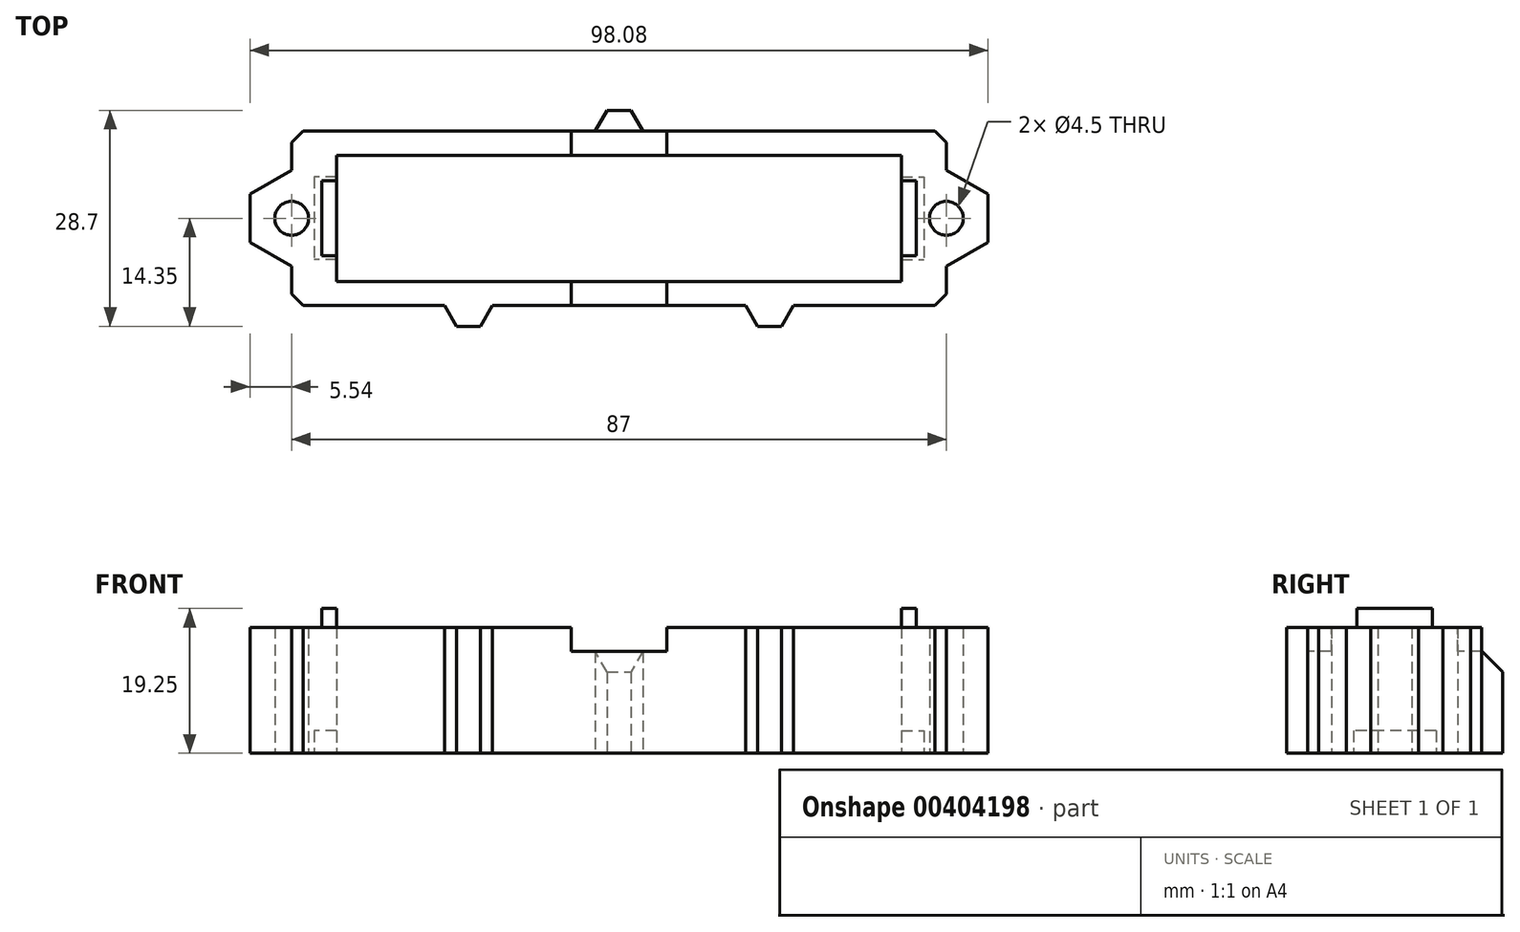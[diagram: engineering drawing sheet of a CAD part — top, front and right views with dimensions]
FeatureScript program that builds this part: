
annotation { "Feature Type Name" : "Feature", "Feature Type Description" : "" }
export const myFeature = defineFeature(function(context is Context, id is Id, definition is map)
    precondition{}
    {
        {
            var Q0;
            Q0=qCreatedBy(makeId("Top.planeOp"),FACE);
            var sketch = newSketch(context, id + "F0", { "sketchPlane" : qUnion([Q0])});
            skLineSegment(sketch, "E0.bottom", {"start": v(37.5, 8.37) * mm, "end": v(-37.5, 8.37) * mm});
            skLineSegment(sketch, "E0.top", {"start": v(37.5, -8.37) * mm, "end": v(-37.5, -8.37) * mm});
            skLineSegment(sketch, "E0.left", {"start": v(37.5, 8.37) * mm, "end": v(37.5, -8.37) * mm});
            skLineSegment(sketch, "E0.right", {"start": v(-37.5, 8.37) * mm, "end": v(-37.5, -8.37) * mm});
            skPoint(sketch, "E0.middle", {"position": v(0, 0) * mm});
            skLineSegment(sketch, "E1.bottom", {"start": v(43.5, 11.57) * mm, "end": v(2.77, 11.57) * mm});
            skLineSegment(sketch, "E1.top", {"start": v(43.5, -11.57) * mm, "end": v(23.2, -11.57) * mm});
            skLineSegment(sketch, "E1.left", {"start": v(43.5, 11.57) * mm, "end": v(43.5, 5.54) * mm});
            skLineSegment(sketch, "E1.right", {"start": v(-43.5, 11.57) * mm, "end": v(-43.5, 6.4) * mm});
            skCircle(sketch, "E2.cCircle", {"center": v(43.5, 0) * mm, "radius": 5.54 * mm, "construction": true});
            skPoint(sketch, "E2.cCircle.centerSnap0", {"position": v(43.5, 0) * mm});
            skLineSegment(sketch, "E2.0", {"start": v(49.04, 3.2) * mm, "end": v(49.04, -3.2) * mm});
            skLineSegment(sketch, "E2.1", {"start": v(49.04, -3.2) * mm, "end": v(43.5, -6.4) * mm});
            skLineSegment(sketch, "E2.2", {"start": v(43.5, -6.4) * mm, "end": v(37.96, -3.2) * mm, "construction": true});
            skLineSegment(sketch, "E2.3", {"start": v(37.96, -3.2) * mm, "end": v(37.96, 3.2) * mm, "construction": true});
            skLineSegment(sketch, "E2.4", {"start": v(37.96, 3.2) * mm, "end": v(43.5, 6.4) * mm, "construction": true});
            skLineSegment(sketch, "E2.5", {"start": v(43.5, 6.4) * mm, "end": v(49.04, 3.2) * mm});
            skPoint(sketch, "E2.0.midPoint", {"position": v(49.04, 0) * mm});
            skLineSegment(sketch, "E3.MirrorCS", {"start": v(-43.5, 6.4) * mm, "end": v(-49.04, 3.2) * mm});
            skLineSegment(sketch, "E4.MirrorCS", {"start": v(-49.04, 3.2) * mm, "end": v(-49.04, -3.2) * mm});
            skLineSegment(sketch, "E5.MirrorCS", {"start": v(-49.04, -3.2) * mm, "end": v(-43.5, -6.4) * mm});
            skLineSegment(sketch, "E6.trimOffspring", {"start": v(-43.5, -6.4) * mm, "end": v(-43.5, -11.57) * mm});
            skLineSegment(sketch, "E7.trimOffspring", {"start": v(43.5, -5.54) * mm, "end": v(43.5, -11.57) * mm});
            skCircle(sketch, "E8.cCircle", {"center": v(0, 11.57) * mm, "radius": 2.77 * mm, "construction": true});
            skLineSegment(sketch, "E8.0", {"start": v(-1.6, 14.35) * mm, "end": v(1.6, 14.35) * mm});
            skLineSegment(sketch, "E8.1", {"start": v(1.6, 14.35) * mm, "end": v(3.2, 11.57) * mm});
            skLineSegment(sketch, "E8.2", {"start": v(3.2, 11.57) * mm, "end": v(1.6, 8.8) * mm, "construction": true});
            skLineSegment(sketch, "E8.3", {"start": v(1.6, 8.8) * mm, "end": v(-1.6, 8.8) * mm, "construction": true});
            skLineSegment(sketch, "E8.4", {"start": v(-1.6, 8.8) * mm, "end": v(-3.2, 11.57) * mm, "construction": true});
            skLineSegment(sketch, "E8.5", {"start": v(-3.2, 11.57) * mm, "end": v(-1.6, 14.35) * mm});
            skPoint(sketch, "E8.0.midPoint", {"position": v(0, 14.35) * mm});
            skCircle(sketch, "E9.cCircle", {"center": v(-20, -11.57) * mm, "radius": 2.77 * mm, "construction": true});
            skLineSegment(sketch, "E9.0", {"start": v(-18.4, -14.35) * mm, "end": v(-21.6, -14.35) * mm});
            skLineSegment(sketch, "E9.1", {"start": v(-21.6, -14.35) * mm, "end": v(-23.2, -11.57) * mm});
            skLineSegment(sketch, "E9.2", {"start": v(-23.2, -11.57) * mm, "end": v(-21.6, -8.8) * mm, "construction": true});
            skLineSegment(sketch, "E9.3", {"start": v(-21.6, -8.8) * mm, "end": v(-18.4, -8.8) * mm, "construction": true});
            skLineSegment(sketch, "E9.4", {"start": v(-18.4, -8.8) * mm, "end": v(-16.8, -11.57) * mm, "construction": true});
            skLineSegment(sketch, "E9.5", {"start": v(-16.8, -11.57) * mm, "end": v(-18.4, -14.35) * mm});
            skPoint(sketch, "E9.0.midPoint", {"position": v(-20, -14.35) * mm});
            skLineSegment(sketch, "E10.MirrorCS", {"start": v(16.8, -11.57) * mm, "end": v(18.4, -14.35) * mm});
            skLineSegment(sketch, "E11.MirrorCS", {"start": v(21.6, -14.35) * mm, "end": v(23.2, -11.57) * mm});
            skLineSegment(sketch, "E12.MirrorCS", {"start": v(18.4, -14.35) * mm, "end": v(21.6, -14.35) * mm});
            skLineSegment(sketch, "E13.trimOffspring", {"start": v(16.8, -11.57) * mm, "end": v(-17.23, -11.57) * mm});
            skLineSegment(sketch, "E14.trimOffspring", {"start": v(-22.77, -11.57) * mm, "end": v(-43.5, -11.57) * mm});
            skLineSegment(sketch, "E15.trimOffspring", {"start": v(-2.77, 11.57) * mm, "end": v(-43.5, 11.57) * mm});
            skCircle(sketch, "E16", {"center": v(43.5, 0) * mm, "radius": 2.25 * mm});
            skCircle(sketch, "E17.MirrorC", {"center": v(-43.5, 0) * mm, "radius": 2.25 * mm});
            skSolve(sketch);
        }
        {
            var Q0;
            Q0=qSketchRegion(id+"F0",true);
            extrude(context, id + "F1", {"entities" : qUnion([Q0]), "depth" : 16.75 * mm});
        }
        {
            var Q0;
            Q0=makeQuery(id+"F1.opExtrude","SWEPT_EDGE",EDGE,{"disambiguationData":[OSD([sQuery(id+"F0.wireOp",EDGE,"E1.right"),sQuery(id+"F0.wireOp",EDGE,"E15.trimOffspring")])]});
            var Q1;
            Q1=makeQuery(id+"F1.opExtrude","SWEPT_EDGE",EDGE,{"disambiguationData":[OSD([sQuery(id+"F0.wireOp",EDGE,"E1.bottom"),sQuery(id+"F0.wireOp",EDGE,"E1.left")])]});
            var Q2;
            Q2=makeQuery(id+"F1.opExtrude","SWEPT_EDGE",EDGE,{"disambiguationData":[OSD([sQuery(id+"F0.wireOp",EDGE,"E1.top"),sQuery(id+"F0.wireOp",EDGE,"E7.trimOffspring")])]});
            var Q3;
            Q3=makeQuery(id+"F1.opExtrude","SWEPT_EDGE",EDGE,{"disambiguationData":[OSD([sQuery(id+"F0.wireOp",EDGE,"E6.trimOffspring"),sQuery(id+"F0.wireOp",EDGE,"E14.trimOffspring")])]});
            var Q4;
            Q4=makeQuery(id+"FqGxmhCherfDVOV_1.opExtrude","SWEPT_EDGE",EDGE,{"disambiguationData":[OSD([sQuery(id+"FbWVWexePYxeVdp_1.wireOp",EDGE,"DEU2wYtO-tHXI-QKIs-nlWb-i6qmyh1Z6pCu.bottom"),sQuery(id+"FbWVWexePYxeVdp_1.wireOp",EDGE,"DEU2wYtO-tHXI-QKIs-nlWb-i6qmyh1Z6pCu.right")])]});
            var Q5;
            Q5=makeQuery(id+"FqGxmhCherfDVOV_1.opExtrude","SWEPT_EDGE",EDGE,{"disambiguationData":[OSD([sQuery(id+"FbWVWexePYxeVdp_1.wireOp",EDGE,"DEU2wYtO-tHXI-QKIs-nlWb-i6qmyh1Z6pCu.bottom"),sQuery(id+"FbWVWexePYxeVdp_1.wireOp",EDGE,"DEU2wYtO-tHXI-QKIs-nlWb-i6qmyh1Z6pCu.left")])]});
            var Q6;
            Q6=makeQuery(id+"FqGxmhCherfDVOV_1.opExtrude","SWEPT_EDGE",EDGE,{"disambiguationData":[OSD([sQuery(id+"FbWVWexePYxeVdp_1.wireOp",EDGE,"DEU2wYtO-tHXI-QKIs-nlWb-i6qmyh1Z6pCu.top"),sQuery(id+"FbWVWexePYxeVdp_1.wireOp",EDGE,"f3f75a21-f88d-41ef-b49e-168493a3c54c.trimOffspring")])]});
            var Q7;
            Q7=makeQuery(id+"FqGxmhCherfDVOV_1.opExtrude","SWEPT_EDGE",EDGE,{"disambiguationData":[OSD([sQuery(id+"FbWVWexePYxeVdp_1.wireOp",EDGE,"DEU2wYtO-tHXI-QKIs-nlWb-i6qmyh1Z6pCu.top"),sQuery(id+"FbWVWexePYxeVdp_1.wireOp",EDGE,"1a49d25c-86bc-4509-88f6-b9e7389082c9.trimOffspring")])]});
            chamfer(context, id + "F2", {"entities" : qUnion([Q0, Q1, Q2, Q3, Q4, Q5, Q6, Q7]), "width" : 1.5 * mm, "tangentPropagation" : true});
        }
        {
            var Q0;
            Q0=qCreatedBy(makeId("Top.planeOp"),FACE);
            var sketch = newSketch(context, id + "F3", { "sketchPlane" : qUnion([Q0])});
            skLineSegment(sketch, "E18.bottom", {"start": v(-37.5, 5.5) * mm, "end": v(-40.5, 5.5) * mm});
            skLineSegment(sketch, "E18.top", {"start": v(-37.5, -5.5) * mm, "end": v(-40.5, -5.5) * mm});
            skLineSegment(sketch, "E18.left", {"start": v(-37.5, 5.5) * mm, "end": v(-37.5, -5.5) * mm});
            skLineSegment(sketch, "E18.right", {"start": v(-40.5, 5.5) * mm, "end": v(-40.5, -5.5) * mm});
            skPoint(sketch, "E18.middle", {"position": v(-39, 0) * mm});
            skLineSegment(sketch, "E19.MirrorCS", {"start": v(37.5, 5.5) * mm, "end": v(40.5, 5.5) * mm});
            skLineSegment(sketch, "E20.MirrorCS", {"start": v(37.5, -5.5) * mm, "end": v(40.5, -5.5) * mm});
            skLineSegment(sketch, "E21.MirrorCS", {"start": v(37.5, 5.5) * mm, "end": v(37.5, -5.5) * mm});
            skLineSegment(sketch, "E22.MirrorCS", {"start": v(40.5, 5.5) * mm, "end": v(40.5, -5.5) * mm});
            skPoint(sketch, "E23.MirrorP", {"position": v(39, 0) * mm});
            skSolve(sketch);
        }
        {
            var Q0;
            Q0=qSketchRegion(id+"F3",true);
            extrude(context, id + "F4", {"entities" : qUnion([Q0]), "operationType" : NewBodyOperationType.REMOVE, "depth" : 3 * mm});
        }
        {
            var Q0;
            Q0=makeQuery(id+"F1.opExtrude","CAP_FACE",FACE,{"disambiguationData":[OSD([sQuery(id+"F0.wireOp",EDGE,"E0.bottom"),sQuery(id+"F0.wireOp",EDGE,"E0.top"),sQuery(id+"F0.wireOp",EDGE,"E0.left"),sQuery(id+"F0.wireOp",EDGE,"E0.right"),sQuery(id+"F0.wireOp",EDGE,"E1.bottom"),sQuery(id+"F0.wireOp",EDGE,"E1.top"),sQuery(id+"F0.wireOp",EDGE,"E1.left"),sQuery(id+"F0.wireOp",EDGE,"E1.right"),sQuery(id+"F0.wireOp",EDGE,"E2.0"),sQuery(id+"F0.wireOp",EDGE,"E2.1"),sQuery(id+"F0.wireOp",EDGE,"E2.5"),sQuery(id+"F0.wireOp",EDGE,"E3.MirrorCS"),sQuery(id+"F0.wireOp",EDGE,"E4.MirrorCS"),sQuery(id+"F0.wireOp",EDGE,"E5.MirrorCS"),sQuery(id+"F0.wireOp",EDGE,"E6.trimOffspring"),sQuery(id+"F0.wireOp",EDGE,"E7.trimOffspring"),sQuery(id+"F0.wireOp",EDGE,"E8.0"),sQuery(id+"F0.wireOp",EDGE,"E8.1"),sQuery(id+"F0.wireOp",EDGE,"E8.5"),sQuery(id+"F0.wireOp",EDGE,"E9.0"),sQuery(id+"F0.wireOp",EDGE,"E9.1"),sQuery(id+"F0.wireOp",EDGE,"E9.5"),sQuery(id+"F0.wireOp",EDGE,"E10.MirrorCS"),sQuery(id+"F0.wireOp",EDGE,"E11.MirrorCS"),sQuery(id+"F0.wireOp",EDGE,"E12.MirrorCS"),sQuery(id+"F0.wireOp",EDGE,"E13.trimOffspring"),sQuery(id+"F0.wireOp",EDGE,"E14.trimOffspring"),sQuery(id+"F0.wireOp",EDGE,"E15.trimOffspring"),sQuery(id+"F0.wireOp",EDGE,"E16"),sQuery(id+"F0.wireOp",EDGE,"E17.MirrorC")])],"isStart":false});
            var sketch = newSketch(context, id + "F5", { "sketchPlane" : qUnion([Q0])});
            skLineSegment(sketch, "E24.bottom", {"start": v(-37.5, 5) * mm, "end": v(-39.5, 5) * mm});
            skLineSegment(sketch, "E24.top", {"start": v(-37.5, -5) * mm, "end": v(-39.5, -5) * mm});
            skLineSegment(sketch, "E24.left", {"start": v(-37.5, 5) * mm, "end": v(-37.5, -5) * mm});
            skLineSegment(sketch, "E24.right", {"start": v(-39.5, 5) * mm, "end": v(-39.5, -5) * mm});
            skPoint(sketch, "E24.middle", {"position": v(-38.5, 0) * mm});
            skPoint(sketch, "E24.middle.positionSnap0", {"position": v(-49.04, 0) * mm});
            skPoint(sketch, "E24.centerSnap0", {"position": v(-49.04, 0) * mm});
            skLineSegment(sketch, "E25.MirrorCS", {"start": v(37.5, 5) * mm, "end": v(39.5, 5) * mm});
            skLineSegment(sketch, "E26.MirrorCS", {"start": v(37.5, -5) * mm, "end": v(39.5, -5) * mm});
            skPoint(sketch, "E27.MirrorP", {"position": v(38.5, 0) * mm});
            skLineSegment(sketch, "E28.MirrorCS", {"start": v(39.5, 5) * mm, "end": v(39.5, -5) * mm});
            skLineSegment(sketch, "E29.MirrorCS", {"start": v(37.5, 5) * mm, "end": v(37.5, -5) * mm});
            skSolve(sketch);
        }
        {
            var Q0;
            Q0=qSketchRegion(id+"F5",true);
            extrude(context, id + "F6", {"entities" : qUnion([Q0]), "operationType" : NewBodyOperationType.ADD, "depth" : 2.5 * mm});
        }
        {
            var Q0;
            Q0=makeQuery(id+"F1.opExtrude","SWEPT_FACE",FACE,{"disambiguationData":[OSD([sQuery(id+"F0.wireOp",EDGE,"E13.trimOffspring")])]});
            var sketch = newSketch(context, id + "F7", { "sketchPlane" : qUnion([Q0])});
            skLineSegment(sketch, "E30.bottom", {"start": v(6.35, 13.55) * mm, "end": v(-6.35, 13.55) * mm});
            skLineSegment(sketch, "E30.top", {"start": v(6.35, 19.95) * mm, "end": v(-6.35, 19.95) * mm});
            skLineSegment(sketch, "E30.left", {"start": v(6.35, 13.55) * mm, "end": v(6.35, 19.95) * mm});
            skLineSegment(sketch, "E30.right", {"start": v(-6.35, 13.55) * mm, "end": v(-6.35, 19.95) * mm});
            skPoint(sketch, "E30.middle", {"position": v(0, 16.75) * mm});
            skSolve(sketch);
        }
        {
            var Q0;
            Q0 = qSketchRegion(id + "F7", true);
            extrude(context, id + "F8", {"entities" : qUnion([Q0]), "operationType" : NewBodyOperationType.REMOVE, "endBound" : BoundingType.THROUGH_ALL, "oppositeDirection" : true, "depth" : 5 * mm});
        }
        {
            var Q0;
            Q0=makeQuery(id+"F8.boolean.opBoolean","INTERSECT",EDGE,{"derivedFrom":[makeQuery(id+"F1.opExtrude","SWEPT_FACE",FACE,{"disambiguationData":[OSD([sQuery(id+"F0.wireOp",EDGE,"E8.0")])]}),makeQuery(id+"F8.opExtrude","SWEPT_FACE",FACE,{"disambiguationData":[OSD([sQuery(id+"F7.wireOp",EDGE,"E30.bottom")])]})]});
            chamfer(context, id + "F9", {"entities" : qUnion([Q0]), "width" : 2.75 * mm, "tangentPropagation" : true});
        }
    });
